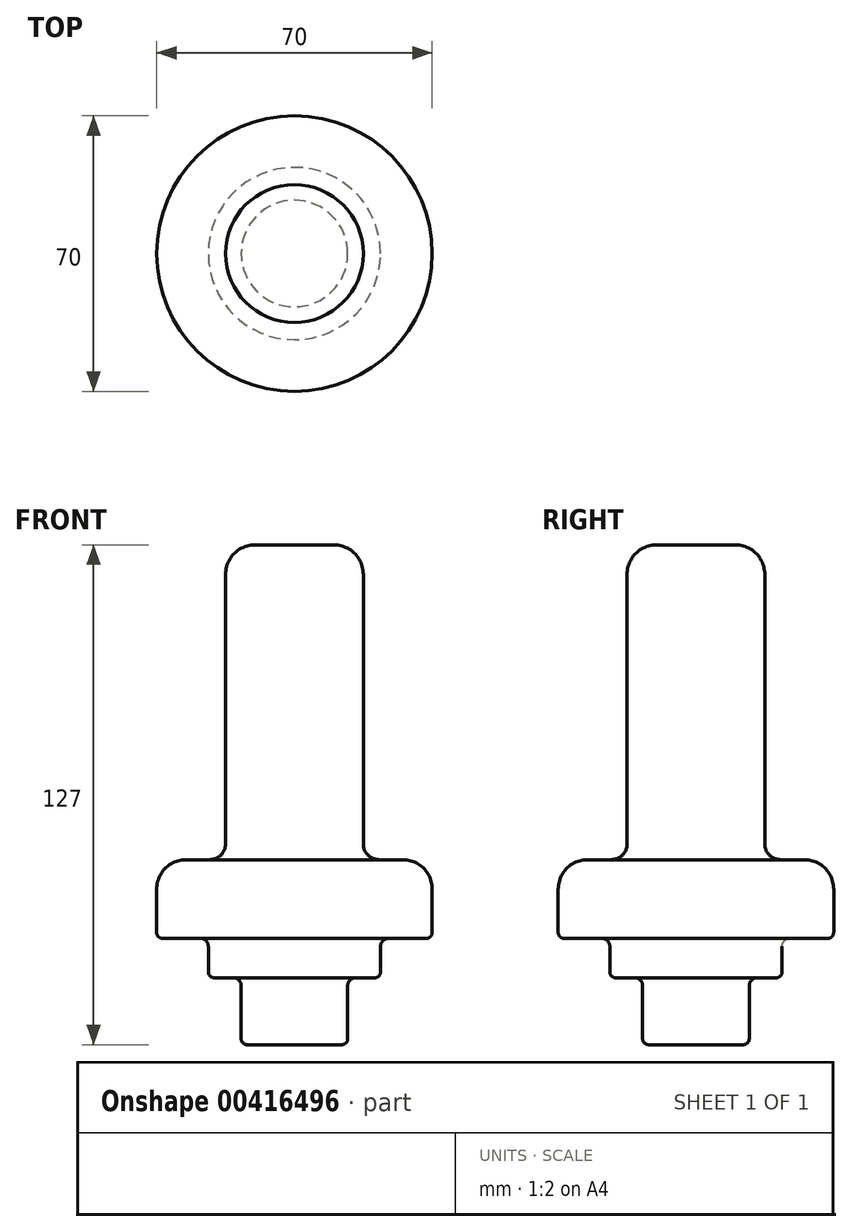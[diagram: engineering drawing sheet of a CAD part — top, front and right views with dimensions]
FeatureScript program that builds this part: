
annotation { "Feature Type Name" : "Feature", "Feature Type Description" : "" }
export const myFeature = defineFeature(function(context is Context, id is Id, definition is map)
    precondition{}
    {
        {
            var Q0;
            Q0=qCreatedBy(makeId("Front.planeOp"),FACE);
            var sketch = newSketch(context, id + "F0", { "sketchPlane" : qUnion([Q0])});
            skLineSegment(sketch, "E0.bottom", {"start": v(0, 0) * mm, "end": v(-12.04, 0) * mm});
            skLineSegment(sketch, "E0.top", {"start": v(0, 17) * mm, "end": v(-14.54, 17) * mm});
            skLineSegment(sketch, "E0.left", {"start": v(0, 0) * mm, "end": v(0, 17) * mm});
            skLineSegment(sketch, "E0.right", {"start": v(-13.54, 1.5) * mm, "end": v(-13.54, 15) * mm});
            skLineSegment(sketch, "E1.bottom", {"start": v(-15.54, 17) * mm, "end": v(-20.38, 17) * mm});
            skLineSegment(sketch, "E1.top", {"start": v(0, 27) * mm, "end": v(-22.38, 27) * mm});
            skLineSegment(sketch, "E1.left", {"start": v(0, 17) * mm, "end": v(0, 27) * mm});
            skLineSegment(sketch, "E1.right", {"start": v(-21.88, 18.5) * mm, "end": v(-21.88, 25) * mm});
            skLineSegment(sketch, "E2.bottom", {"start": v(-23.88, 27) * mm, "end": v(-33.5, 27) * mm});
            skLineSegment(sketch, "E2.top", {"start": v(-21.5, 47) * mm, "end": v(-27.5, 47) * mm});
            skLineSegment(sketch, "E2.left", {"start": v(0, 27) * mm, "end": v(0, 47) * mm});
            skLineSegment(sketch, "E2.right", {"start": v(-35, 28.5) * mm, "end": v(-35, 39.5) * mm});
            skPoint(sketch, "E3.oppositeSnap0", {"position": v(-17.5, 47) * mm});
            skLineSegment(sketch, "E3.top", {"start": v(0, 127) * mm, "end": v(-10, 127) * mm});
            skLineSegment(sketch, "E3.left", {"start": v(0, 47) * mm, "end": v(0, 127) * mm});
            skLineSegment(sketch, "E3.right", {"start": v(-17.5, 51) * mm, "end": v(-17.5, 119.5) * mm});
            skPoint(sketch, "E4.visualSharp", {"position": v(-17.5, 127) * mm});
            skArc(sketch, "E4.filletArc", {"start": v(-10, 127) * mm, "mid": v(-15.3, 124.8) * mm, "end": v(-17.5, 119.5) * mm});
            skPoint(sketch, "E5.visualSharp", {"position": v(-35, 47) * mm});
            skArc(sketch, "E5.filletArc", {"start": v(-27.5, 47) * mm, "mid": v(-32.8, 44.8) * mm, "end": v(-35, 39.5) * mm});
            skPoint(sketch, "E6.visualSharp", {"position": v(-35, 27) * mm});
            skArc(sketch, "E6.filletArc", {"start": v(-35, 28.5) * mm, "mid": v(-34.56, 27.44) * mm, "end": v(-33.5, 27) * mm});
            skPoint(sketch, "E7.visualSharp", {"position": v(-21.88, 17) * mm});
            skArc(sketch, "E7.filletArc", {"start": v(-21.88, 18.5) * mm, "mid": v(-21.44, 17.44) * mm, "end": v(-20.38, 17) * mm});
            skPoint(sketch, "E8.visualSharp", {"position": v(-13.54, 0) * mm});
            skArc(sketch, "E8.filletArc", {"start": v(-13.54, 1.5) * mm, "mid": v(-13.1, 0.44) * mm, "end": v(-12.04, 0) * mm});
            skPoint(sketch, "E9.newPointB", {"position": v(-13.54, 17) * mm});
            skArc(sketch, "E9.filletArc", {"start": v(-13.54, 15) * mm, "mid": v(-14.13, 16.41) * mm, "end": v(-15.54, 17) * mm});
            skArc(sketch, "E10.filletArc", {"start": v(-21.88, 25) * mm, "mid": v(-22.47, 26.41) * mm, "end": v(-23.88, 27) * mm});
            skPoint(sketch, "E11.newPointB", {"position": v(0, 47) * mm});
            skArc(sketch, "E11.filletArc", {"start": v(-21.5, 47) * mm, "mid": v(-18.67, 48.17) * mm, "end": v(-17.5, 51) * mm});
            skLineSegment(sketch, "E12", {"start": v(0, -28.36) * mm, "end": v(0, 131.29) * mm});
            skSolve(sketch);
        }
        {
            var Q0;
            {var subQ1=sQuery(id+"F0.wireOp",EDGE,"E0.bottom");Q0=makeQuery(id+"F0.imprint","IMPRINT",FACE,{"disambiguationData":[TD([[makeQuery(id+"F0.imprint","IMPRINT",EDGE,{"derivedFrom":subQ1}),-1.0]])]});}
            var Q1;
            Q1 = qConstructionFilter(qBodyType(qCreatedBy(id + "F0" ,EDGE), BodyType.WIRE), ConstructionObject.NO);
            var Q2;
            Q2=sQuery(id+"F0.wireOp",EDGE,"E12");
            revolve(context, id + "F1", {"entities" : qUnion([Q0]), "surfaceEntities" : qUnion([Q1]), "axis" : qUnion([Q2]), "revolveType" : RevolveType.FULL});
        }
    });
